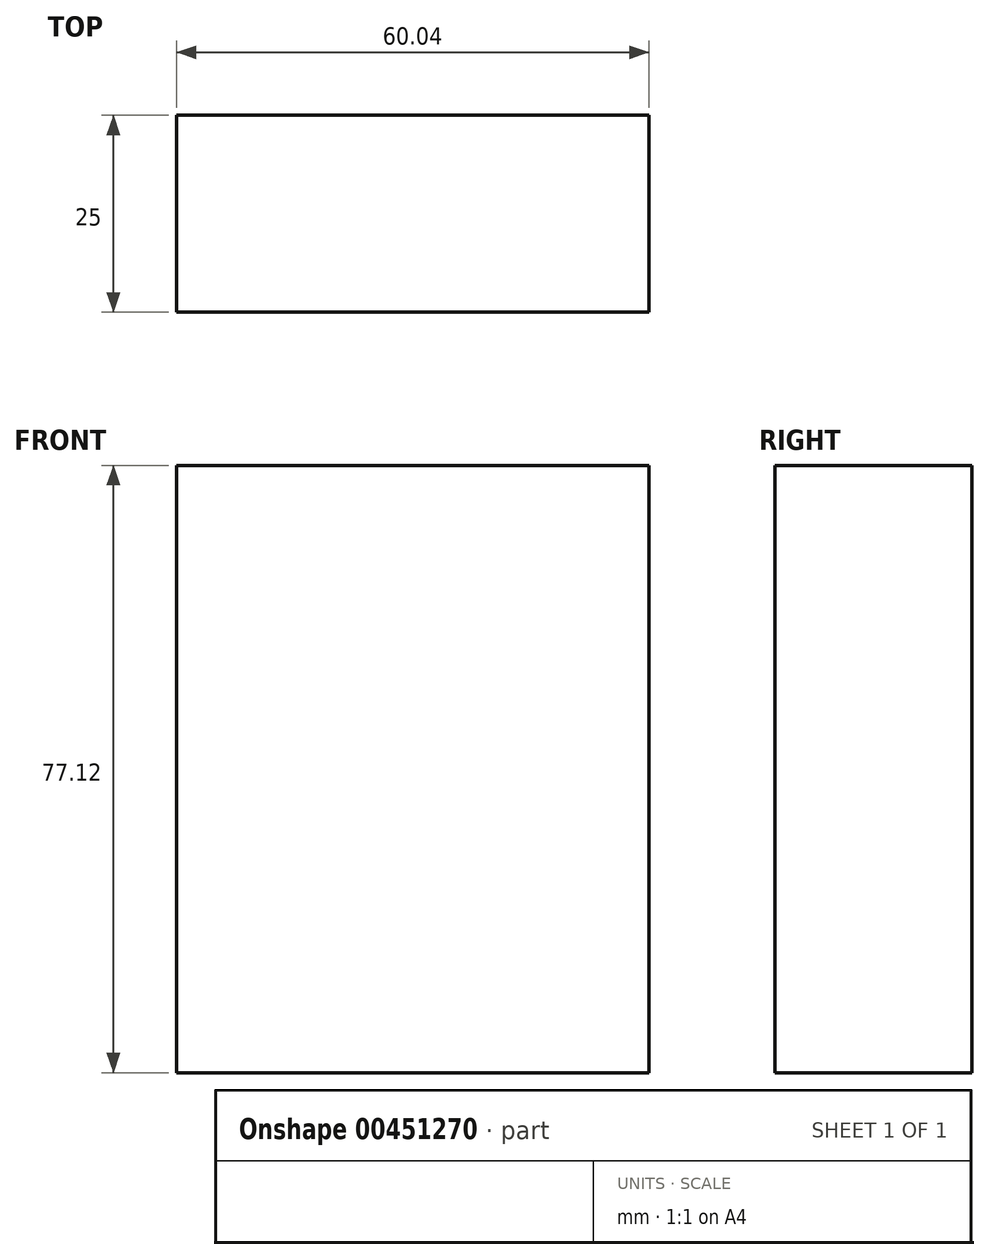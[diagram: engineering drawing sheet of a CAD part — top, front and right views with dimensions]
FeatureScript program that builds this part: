
annotation { "Feature Type Name" : "Feature", "Feature Type Description" : "" }
export const myFeature = defineFeature(function(context is Context, id is Id, definition is map)
    precondition{}
    {
        {
            var Q0;
            Q0=qCreatedBy(makeId("Front.planeOp"),FACE);
            var sketch = newSketch(context, id + "F0", { "sketchPlane" : qUnion([Q0])});
            skLineSegment(sketch, "E0.bottom", {"start": v(-131.12, 23.17) * mm, "end": v(-71.08, 23.17) * mm});
            skLineSegment(sketch, "E0.top", {"start": v(-131.12, -53.95) * mm, "end": v(-71.08, -53.95) * mm});
            skLineSegment(sketch, "E0.left", {"start": v(-131.12, 23.17) * mm, "end": v(-131.12, -53.95) * mm});
            skLineSegment(sketch, "E0.right", {"start": v(-71.08, 23.17) * mm, "end": v(-71.08, -53.95) * mm});
            skSolve(sketch);
        }
        {
            var Q0;
            Q0 = qSketchRegion(id + "F0", true);
            extrude(context, id + "F1", {"entities" : qUnion([Q0]), "depth" : 25 * mm});
        }
    });
